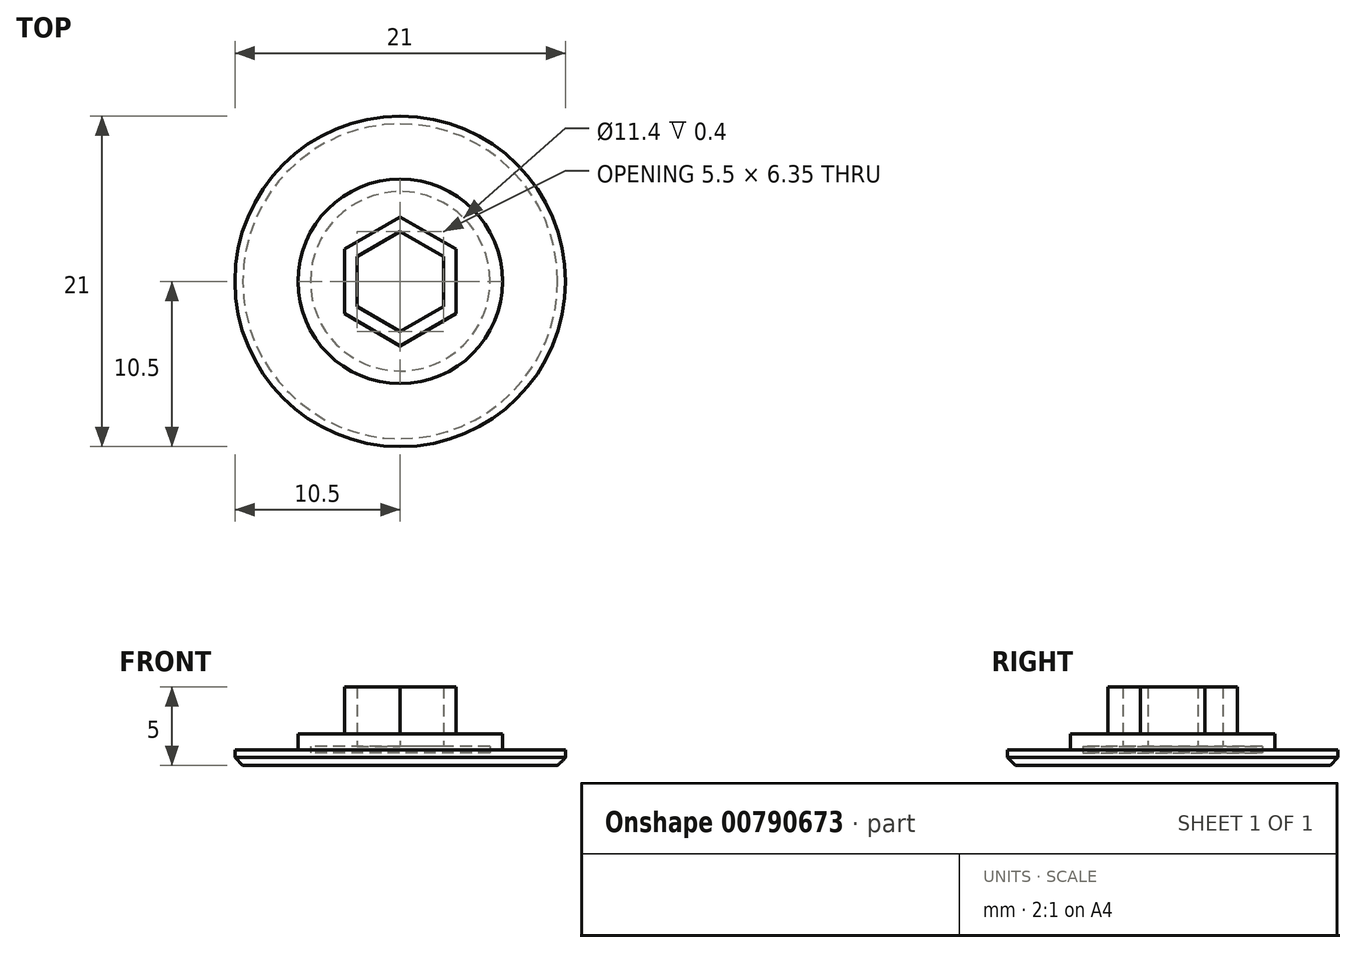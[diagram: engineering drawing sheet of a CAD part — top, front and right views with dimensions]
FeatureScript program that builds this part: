
annotation { "Feature Type Name" : "Feature", "Feature Type Description" : "" }
export const myFeature = defineFeature(function(context is Context, id is Id, definition is map)
    precondition{}
    {
        {
            var Q0;
            Q0=qCreatedBy(makeId("Top.planeOp"),FACE);
            var sketch = newSketch(context, id + "F0", { "sketchPlane" : qUnion([Q0])});
            skCircle(sketch, "E0", {"center": v(0, 0) * mm, "radius": 10.5 * mm});
            skSolve(sketch);
        }
        {
            var Q0;
            Q0=makeQuery(id+"F0.imprint","IMPRINT",FACE,{"disambiguationData":[TD([[makeQuery(id+"F0.imprint","IMPRINT",EDGE,{"derivedFrom":sQuery(id+"F0.wireOp",EDGE,"E0")}),1.0]])]});
            extrude(context, id + "F1", {"entities" : qUnion([Q0]), "depth" : 1 * mm, "offsetDistance" : 25 * mm});
        }
        {
            var Q0;
            {var subQ0=sQuery(id+"F0.wireOp",EDGE,"E0");Q0=makeQuery(id+"FCE4xjLwlJGgTYo_1.boolean.opBoolean","SPLIT",FACE,{"disambiguationData":[TD([makeQuery(id+"F1.opExtrude","SWEPT_FACE",FACE,{"disambiguationData":[OSD([subQ0])]})])],"derivedFrom":makeQuery(id+"F1.opExtrude","CAP_FACE",FACE,{"disambiguationData":[OSD([subQ0])],"isStart":false})});}
            var sketch = newSketch(context, id + "F2", { "sketchPlane" : qUnion([Q0])});
            skCircle(sketch, "E1", {"center": v(0, 0) * mm, "radius": 6.5 * mm});
            skSolve(sketch);
        }
        {
            var Q0;
            Q0=makeQuery(id+"F2.imprint","IMPRINT",FACE,{"disambiguationData":[TD([[makeQuery(id+"F2.imprint","IMPRINT",EDGE,{"derivedFrom":sQuery(id+"F2.wireOp",EDGE,"E1")}),1.0]])]});
            extrude(context, id + "F3", {"entities" : qUnion([Q0]), "operationType" : NewBodyOperationType.ADD, "depth" : 1 * mm, "offsetDistance" : 25 * mm});
        }
        {
            var Q0;
            Q0=makeQuery(id+"F3.opExtrude","CAP_FACE",FACE,{"disambiguationData":[OSD([sQuery(id+"F2.wireOp",EDGE,"E1")])],"isStart":false});
            var sketch = newSketch(context, id + "F4", { "sketchPlane" : qUnion([Q0])});
            skCircle(sketch, "E2.cCircle", {"center": v(0, 0) * mm, "radius": 4.1 * mm, "construction": true});
            skLineSegment(sketch, "E2.0", {"start": v(0, 4.1) * mm, "end": v(3.55, 2.05) * mm});
            skLineSegment(sketch, "E2.1", {"start": v(3.55, 2.05) * mm, "end": v(3.55, -2.05) * mm});
            skLineSegment(sketch, "E2.2", {"start": v(3.55, -2.05) * mm, "end": v(0, -4.1) * mm});
            skLineSegment(sketch, "E2.3", {"start": v(0, -4.1) * mm, "end": v(-3.55, -2.05) * mm});
            skLineSegment(sketch, "E2.4", {"start": v(-3.55, -2.05) * mm, "end": v(-3.55, 2.05) * mm});
            skLineSegment(sketch, "E2.5", {"start": v(-3.55, 2.05) * mm, "end": v(0, 4.1) * mm});
            skSolve(sketch);
        }
        {
            var Q0;
            Q0=makeQuery(id+"F4.imprint","IMPRINT",FACE,{"disambiguationData":[TD([[makeQuery(id+"F4.imprint","IMPRINT",EDGE,{"derivedFrom":sQuery(id+"F4.wireOp",EDGE,"E2.0")}),-1.0]])]});
            extrude(context, id + "F5", {"entities" : qUnion([Q0]), "operationType" : NewBodyOperationType.ADD, "depth" : 3 * mm, "offsetDistance" : 25 * mm});
        }
        {
            var Q0;
            Q0=makeQuery(id+"F5.opExtrude","CAP_FACE",FACE,{"disambiguationData":[OSD([sQuery(id+"F4.wireOp",EDGE,"E2.0"),sQuery(id+"F4.wireOp",EDGE,"E2.1"),sQuery(id+"F4.wireOp",EDGE,"E2.2"),sQuery(id+"F4.wireOp",EDGE,"E2.3"),sQuery(id+"F4.wireOp",EDGE,"E2.4"),sQuery(id+"F4.wireOp",EDGE,"E2.5")])],"isStart":false});
            shell(context, id + "F6", {"entities" : qUnion([Q0]), "thickness" : .8 * mm});
        }
        {
            var Q0;
            Q0=makeQuery(id+"F1.opExtrude","CAP_EDGE",EDGE,{"disambiguationData":[OSD([sQuery(id+"F0.wireOp",EDGE,"E0")])],"isStart":true});
            chamfer(context, id + "F7", {"entities" : qUnion([Q0]), "width" : .5 * mm, "tangentPropagation" : true});
        }
    });
